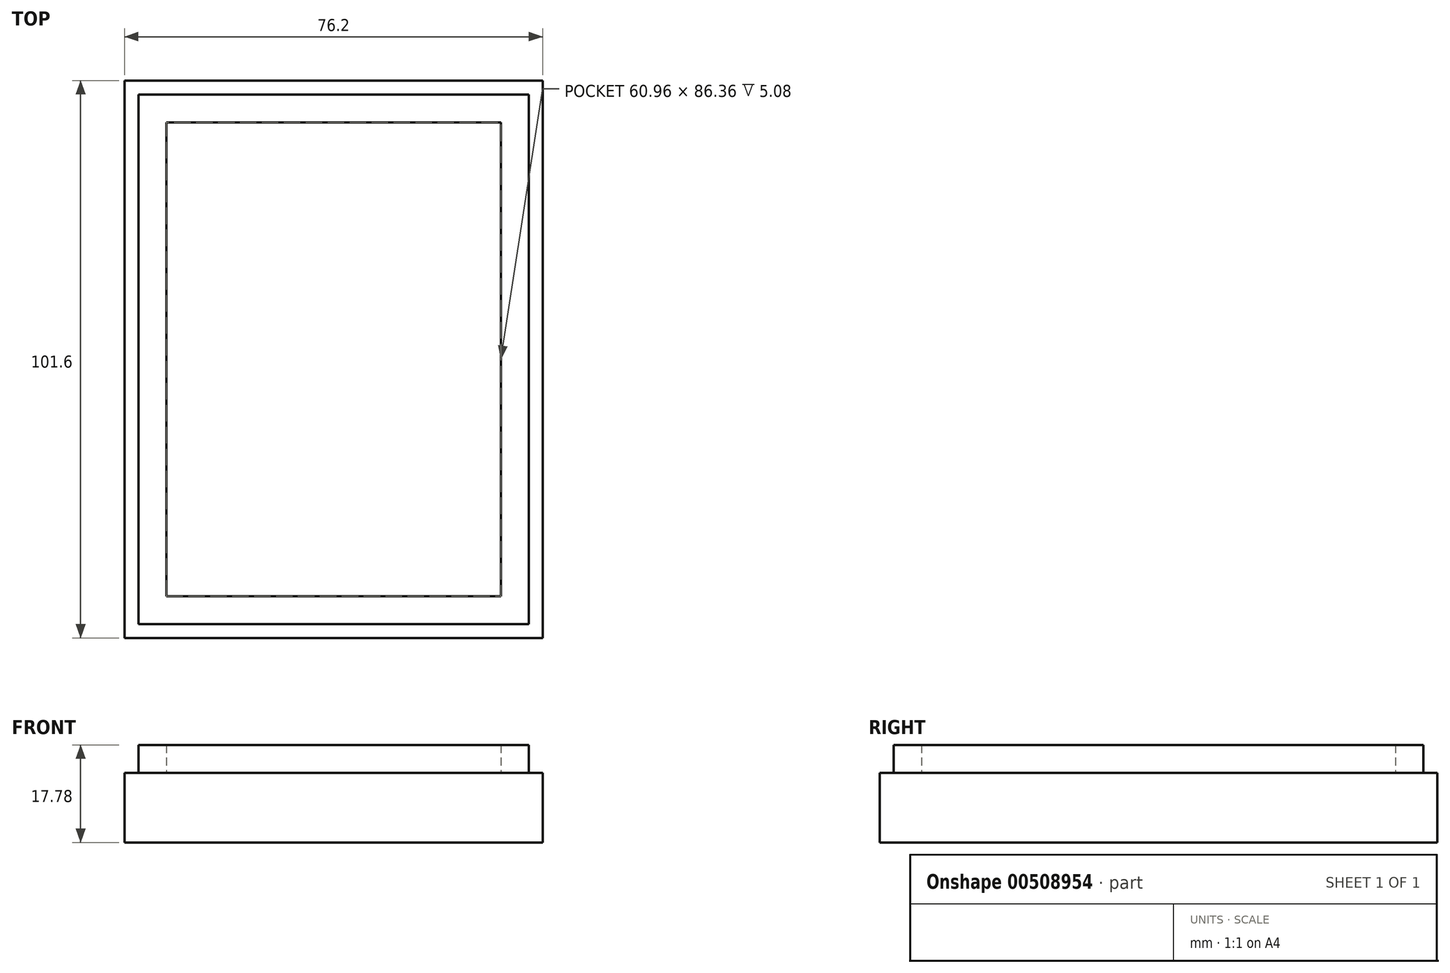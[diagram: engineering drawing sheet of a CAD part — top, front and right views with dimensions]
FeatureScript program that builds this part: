
annotation { "Feature Type Name" : "Feature", "Feature Type Description" : "" }
export const myFeature = defineFeature(function(context is Context, id is Id, definition is map)
    precondition{}
    {
        {
            var Q0;
            Q0=qCreatedBy(makeId("Top.planeOp"),FACE);
            var sketch = newSketch(context, id + "F0", { "sketchPlane" : qUnion([Q0])});
            skLineSegment(sketch, "E0.bottom", {"start": v(0, 0) * mm, "end": v(-76.2, 0) * mm});
            skLineSegment(sketch, "E0.top", {"start": v(0, 101.6) * mm, "end": v(-76.2, 101.6) * mm});
            skLineSegment(sketch, "E0.left", {"start": v(0, 0) * mm, "end": v(0, 101.6) * mm});
            skLineSegment(sketch, "E0.right", {"start": v(-76.2, 0) * mm, "end": v(-76.2, 101.6) * mm});
            skSolve(sketch);
        }
        {
            var Q0;
            Q0=makeQuery(id+"F0.imprint","IMPRINT",FACE,{"disambiguationData":[TD([[makeQuery(id+"F0.imprint","IMPRINT",EDGE,{"derivedFrom":sQuery(id+"F0.wireOp",EDGE,"E0.bottom")}),-1.0]])]});
            extrude(context, id + "F1", {"entities" : qUnion([Q0]), "oppositeDirection" : true, "depth" : 12.7 * mm});
        }
        {
            var Q0;
            Q0=makeQuery(id+"F1.opExtrude","CAP_FACE",FACE,{"disambiguationData":[OSD([sQuery(id+"F0.wireOp",EDGE,"E0.bottom"),sQuery(id+"F0.wireOp",EDGE,"E0.top"),sQuery(id+"F0.wireOp",EDGE,"E0.left"),sQuery(id+"F0.wireOp",EDGE,"E0.right")])],"isStart":true});
            var sketch = newSketch(context, id + "F2", { "sketchPlane" : qUnion([Q0])});
            skLineSegment(sketch, "E1.bottom", {"start": v(-2.54, 2.54) * mm, "end": v(-73.66, 2.54) * mm});
            skLineSegment(sketch, "E1.top", {"start": v(-2.54, 99.06) * mm, "end": v(-73.66, 99.06) * mm});
            skLineSegment(sketch, "E1.left", {"start": v(-2.54, 2.54) * mm, "end": v(-2.54, 99.06) * mm});
            skLineSegment(sketch, "E1.right", {"start": v(-73.66, 2.54) * mm, "end": v(-73.66, 99.06) * mm});
            skLineSegment(sketch, "E2.bottom", {"start": v(-68.58, 93.98) * mm, "end": v(-7.62, 93.98) * mm});
            skLineSegment(sketch, "E2.top", {"start": v(-68.58, 7.62) * mm, "end": v(-7.62, 7.62) * mm});
            skLineSegment(sketch, "E2.left", {"start": v(-68.58, 93.98) * mm, "end": v(-68.58, 7.62) * mm});
            skLineSegment(sketch, "E2.right", {"start": v(-7.62, 93.98) * mm, "end": v(-7.62, 7.62) * mm});
            skSolve(sketch);
        }
        {
            var Q0;
            Q0=makeQuery(id+"F2.imprint","IMPRINT",FACE,{"disambiguationData":[TD([[makeQuery(id+"F2.imprint","IMPRINT",EDGE,{"derivedFrom":sQuery(id+"F2.wireOp",EDGE,"E1.bottom")}),-1.0]])]});
            extrude(context, id + "F3", {"entities" : qUnion([Q0]), "operationType" : NewBodyOperationType.ADD, "depth" : 5.08 * mm});
        }
    });
